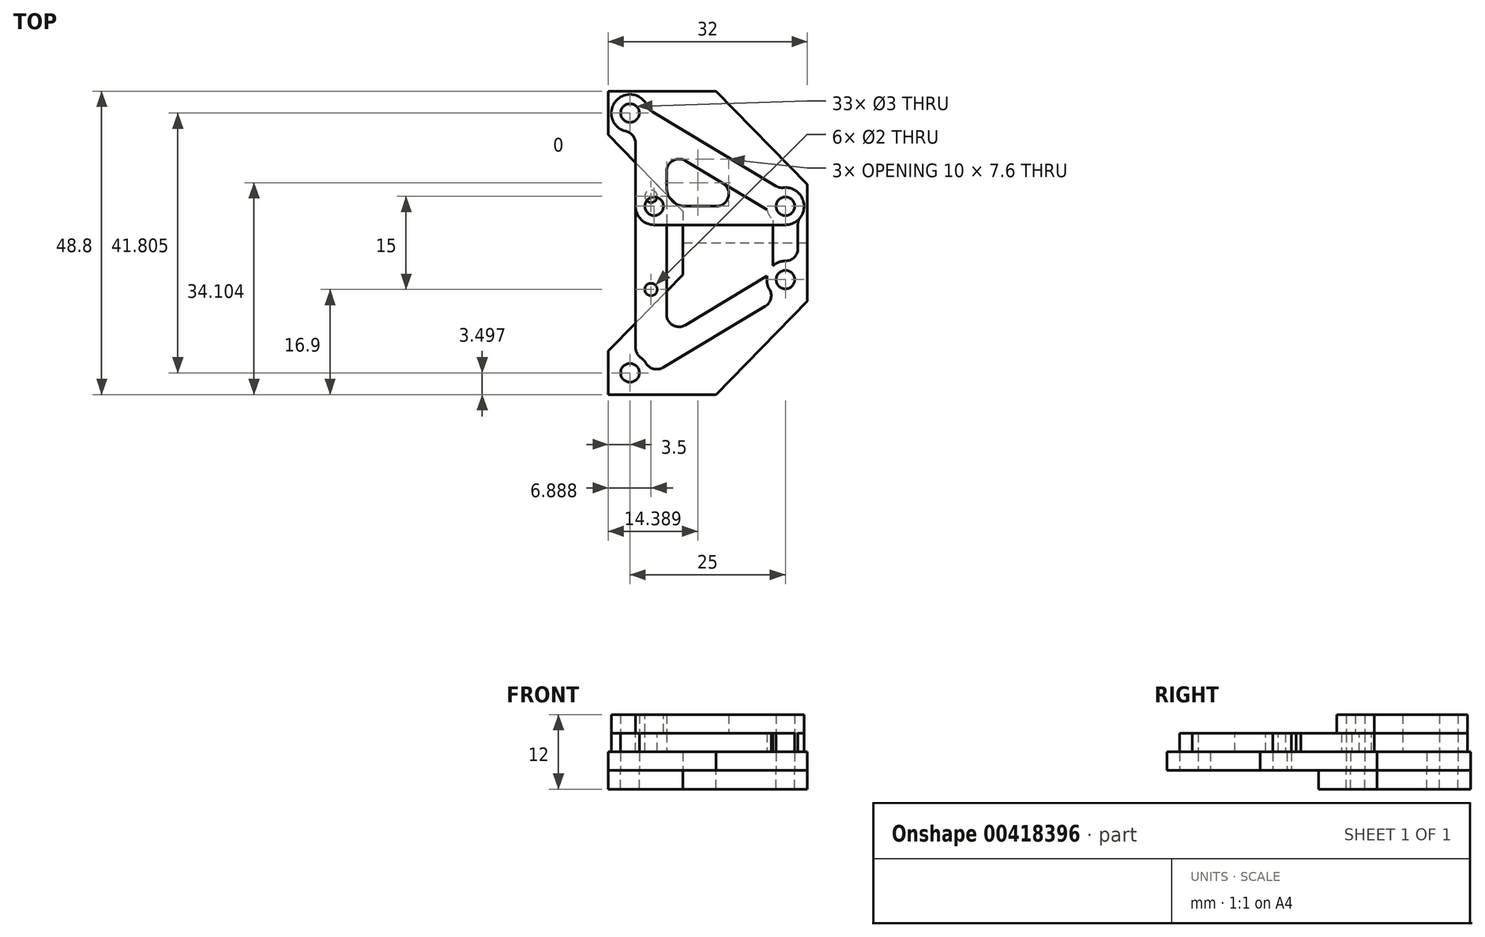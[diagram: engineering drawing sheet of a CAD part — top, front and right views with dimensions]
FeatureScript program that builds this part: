
annotation { "Feature Type Name" : "Feature", "Feature Type Description" : "" }
export const myFeature = defineFeature(function(context is Context, id is Id, definition is map)
    precondition{}
    {
        {
            var Q0;
            Q0=qCreatedBy(makeId("Top.planeOp"),FACE);
            var sketch = newSketch(context, id + "F0", { "sketchPlane" : qUnion([Q0])});
            skCircle(sketch, "E0", {"center": v(0, 20.9) * mm, "radius": 1.5 * mm});
            skCircle(sketch, "E1", {"center": v(25, 5.9) * mm, "radius": 1.5 * mm});
            skCircle(sketch, "E2.MirrorC", {"center": v(0, -20.9) * mm, "radius": 1.5 * mm});
            skCircle(sketch, "E3.MirrorC", {"center": v(25, -5.9) * mm, "radius": 1.5 * mm});
            skLineSegment(sketch, "E4", {"start": v(8.5, 5.12) * mm, "end": v(-3.5, 17.4) * mm});
            skLineSegment(sketch, "E5", {"start": v(-3.5, 17.4) * mm, "end": v(-3.5, 24.4) * mm});
            skLineSegment(sketch, "E6", {"start": v(-3.5, 24.4) * mm, "end": v(13.85, 24.4) * mm});
            skLineSegment(sketch, "E7", {"start": v(13.85, 24.4) * mm, "end": v(28.5, 9.4) * mm});
            skLineSegment(sketch, "E8", {"start": v(28.5, 9.4) * mm, "end": v(28.5, 0) * mm});
            skLineSegment(sketch, "E9.MirrorCS", {"start": v(8.5, -5.12) * mm, "end": v(-3.5, -17.4) * mm});
            skLineSegment(sketch, "E10.MirrorCS", {"start": v(-3.5, -17.4) * mm, "end": v(-3.5, -24.4) * mm});
            skLineSegment(sketch, "E11.MirrorCS", {"start": v(-3.5, -24.4) * mm, "end": v(13.85, -24.4) * mm});
            skLineSegment(sketch, "E12.MirrorCS", {"start": v(13.85, -24.4) * mm, "end": v(28.5, -9.4) * mm});
            skLineSegment(sketch, "E13.MirrorCS", {"start": v(28.5, -9.4) * mm, "end": v(28.5, 0) * mm});
            skLineSegment(sketch, "E14", {"start": v(8.5, 5.12) * mm, "end": v(8.5, -5.12) * mm});
            skPoint(sketch, "E15.orphan", {"position": v(13.5, 0) * mm});
            skLineSegment(sketch, "E16", {"start": v(8.5, 0) * mm, "end": v(28.5, 0) * mm});
            skSolve(sketch);
        }
        {
            var Q0;
            Q0=qSketchRegion(id+"F0",true);
            extrude(context, id + "F1", {"entities" : qUnion([Q0]), "depth" : 3 * mm, "offsetDistance" : 25 * mm});
        }
        {
            var Q0;
            Q0=makeQuery(id+"F0.imprint","IMPRINT",FACE,{"disambiguationData":[TD([[makeQuery(id+"F0.imprint","IMPRINT",EDGE,{"derivedFrom":sQuery(id+"F0.wireOp",EDGE,"E0")}),-1.0]])]});
            extrude(context, id + "F2", {"entities" : qUnion([Q0]), "oppositeDirection" : true, "depth" : 3 * mm, "offsetDistance" : 25 * mm});
        }
        {
            var Q0;
            Q0=makeQuery(id+"F1.opExtrude","CAP_FACE",FACE,{"disambiguationData":[OSD([sQuery(id+"F0.wireOp",EDGE,"E0"),sQuery(id+"F0.wireOp",EDGE,"E1"),sQuery(id+"F0.wireOp",EDGE,"E2.MirrorC"),sQuery(id+"F0.wireOp",EDGE,"E3.MirrorC"),sQuery(id+"F0.wireOp",EDGE,"E4"),sQuery(id+"F0.wireOp",EDGE,"E5"),sQuery(id+"F0.wireOp",EDGE,"E6"),sQuery(id+"F0.wireOp",EDGE,"E7"),sQuery(id+"F0.wireOp",EDGE,"E8"),sQuery(id+"F0.wireOp",EDGE,"E9.MirrorCS"),sQuery(id+"F0.wireOp",EDGE,"E10.MirrorCS"),sQuery(id+"F0.wireOp",EDGE,"E11.MirrorCS"),sQuery(id+"F0.wireOp",EDGE,"E12.MirrorCS"),sQuery(id+"F0.wireOp",EDGE,"E13.MirrorCS"),sQuery(id+"F0.wireOp",EDGE,"E14")])],"isStart":false});
            var sketch = newSketch(context, id + "F3", { "sketchPlane" : qUnion([Q0])});
            skCircle(sketch, "E17.0", {"center": v(0, 20.9) * mm, "radius": 1.5 * mm});
            skCircle(sketch, "E18.0", {"center": v(25, 5.9) * mm, "radius": 1.5 * mm});
            skCircle(sketch, "E19", {"center": v(0, 20.9) * mm, "radius": 3 * mm});
            skCircle(sketch, "E20", {"center": v(25, 5.9) * mm, "radius": 3 * mm});
            skPoint(sketch, "E21", {"position": v(1.5, 20.9) * mm});
            skPoint(sketch, "E22", {"position": v(3, 20.9) * mm});
            skPoint(sketch, "E23", {"position": v(26.5, 5.9) * mm});
            skPoint(sketch, "E24", {"position": v(28, 5.9) * mm});
            skLineSegment(sketch, "E25", {"start": v(0, 20.9) * mm, "end": v(25, 5.9) * mm, "construction": true});
            skCircle(sketch, "E26.0", {"center": v(25, -5.9) * mm, "radius": 1.5 * mm});
            skLineSegment(sketch, "E27", {"start": v(25, 5.9) * mm, "end": v(25, -5.9) * mm, "construction": true});
            skCircle(sketch, "E28.MirrorC", {"center": v(25, -5.9) * mm, "radius": 3 * mm});
            skCircle(sketch, "E29.MirrorC", {"center": v(0, -20.9) * mm, "radius": 3 * mm});
            skLineSegment(sketch, "E30", {"start": v(23, 3.67) * mm, "end": v(23, -3.67) * mm});
            skLineSegment(sketch, "E31.MirrorCS", {"start": v(27, 3.67) * mm, "end": v(27, -3.67) * mm});
            skLineSegment(sketch, "E32", {"start": v(0.89, 18.04) * mm, "end": v(22.05, 5.34) * mm});
            skLineSegment(sketch, "E33.MirrorCS", {"start": v(2.95, 21.47) * mm, "end": v(24.11, 8.77) * mm});
            skLineSegment(sketch, "E34.MirrorCS", {"start": v(0.89, -18.04) * mm, "end": v(22.05, -5.34) * mm});
            skLineSegment(sketch, "E35.MirrorCS", {"start": v(2.95, -21.47) * mm, "end": v(24.11, -8.77) * mm});
            skLineSegment(sketch, "E36", {"start": v(0.89, 18.04) * mm, "end": v(0.89, -18.04) * mm});
            skLineSegment(sketch, "E37", {"start": v(5.89, 15.04) * mm, "end": v(5.89, -15.04) * mm});
            skSolve(sketch);
        }
        {
            var Q0;
            Q0=makeQuery(id+"F3.imprint","IMPRINT",FACE,{"disambiguationData":[TD([[makeQuery(id+"F3.imprint","IMPRINT",EDGE,{"derivedFrom":sQuery(id+"F3.wireOp",EDGE,"E17.0")}),-1.0]])]});
            var Q1;
            Q1=makeQuery(id+"F3.imprint","IMPRINT",FACE,{"disambiguationData":[TD([[makeQuery(id+"F3.imprint","IMPRINT",EDGE,{"derivedFrom":makeQuery(id+"F1.opExtrude","CAP_EDGE",EDGE,{"disambiguationData":[OSD([sQuery(id+"F0.wireOp",EDGE,"E2.MirrorC")])],"isStart":false})}),1.0]])]});
            var Q2;
            {var subQ0=sQuery(id+"F3.wireOp",EDGE,"E30");Q2=makeQuery(id+"F3.imprint","IMPRINT",FACE,{"disambiguationData":[TD([[makeQuery(id+"F3.imprint","IMPRINT",EDGE,{"derivedFrom":subQ0}),1.0]])]});}
            var Q3;
            Q3=makeQuery(id+"F3.imprint","IMPRINT",FACE,{"disambiguationData":[TD([[makeQuery(id+"F3.imprint","IMPRINT",EDGE,{"derivedFrom":sQuery(id+"F3.wireOp",EDGE,"E18.0")}),-1.0]])]});
            var Q4;
            {var subQ6=sQuery(id+"F3.wireOp",EDGE,"E33.MirrorCS");Q4=makeQuery(id+"F3.imprint","IMPRINT",FACE,{"disambiguationData":[TD([[makeQuery(id+"F3.imprint","IMPRINT",EDGE,{"derivedFrom":subQ6}),-1.0]])]});}
            var Q5;
            Q5=makeQuery(id+"F3.imprint","IMPRINT",FACE,{"disambiguationData":[TD([[makeQuery(id+"F3.imprint","IMPRINT",EDGE,{"derivedFrom":sQuery(id+"F3.wireOp",EDGE,"E26.0")}),1.0]])]});
            var Q6;
            {var subQ6=sQuery(id+"F3.wireOp",EDGE,"E35.MirrorCS");Q6=makeQuery(id+"F3.imprint","IMPRINT",FACE,{"disambiguationData":[TD([[makeQuery(id+"F3.imprint","IMPRINT",EDGE,{"derivedFrom":subQ6}),1.0]])]});}
            var Q7;
            {var subQ1=sQuery(id+"F3.wireOp",EDGE,"E32");var subQ3=sQuery(id+"F3.wireOp",EDGE,"E37");var subQ4=makeQuery(id+"F3.imprint","INTERSECT",VERTEX,{"derivedFrom":[subQ1,subQ3]});Q7=makeQuery(id+"F3.imprint","IMPRINT",FACE,{"disambiguationData":[TD([[makeQuery(id+"F3.imprint","IMPRINT",EDGE,{"disambiguationData":[TD([[subQ4,-1.0]])],"derivedFrom":subQ3}),-1.0]])]});}
            var Q8;
            {var subQ1=sQuery(id+"F3.wireOp",EDGE,"E34.MirrorCS");var subQ3=sQuery(id+"F3.wireOp",EDGE,"E37");var subQ4=makeQuery(id+"F3.imprint","INTERSECT",VERTEX,{"derivedFrom":[subQ1,subQ3]});Q8=makeQuery(id+"F3.imprint","IMPRINT",FACE,{"disambiguationData":[TD([[makeQuery(id+"F3.imprint","IMPRINT",EDGE,{"disambiguationData":[TD([[subQ4,1.0]])],"derivedFrom":subQ3}),-1.0]])]});}
            var Q9;
            {var subQ0=sQuery(id+"F3.wireOp",EDGE,"E36");var subQ1=makeQuery(id+"F1.opExtrude","CAP_EDGE",EDGE,{"disambiguationData":[OSD([sQuery(id+"F0.wireOp",EDGE,"E4")])],"isStart":false});var subQ2=makeQuery(id+"F3.imprint","INTERSECT",VERTEX,{"derivedFrom":[subQ1,subQ0]});Q9=makeQuery(id+"F3.imprint","IMPRINT",FACE,{"disambiguationData":[TD([[makeQuery(id+"F3.imprint","IMPRINT",EDGE,{"disambiguationData":[TD([[subQ2,-1.0]])],"derivedFrom":subQ0}),1.0]])]});}
            extrude(context, id + "F4", {"entities" : qUnion([Q0, Q1, Q2, Q3, Q4, Q5, Q6, Q7, Q8, Q9]), "depth" : 3 * mm, "offsetDistance" : 25 * mm});
        }
        {
            var Q0;
            Q0=makeQuery(id+"F4.opExtrude","SWEPT_EDGE",EDGE,{"disambiguationData":[OSD([sQuery(id+"F3.wireOp",EDGE,"E19"),sQuery(id+"F3.wireOp",EDGE,"E32"),sQuery(id+"F3.wireOp",EDGE,"E36")])]});
            var Q1;
            Q1=makeQuery(id+"F4.opExtrude","SWEPT_EDGE",EDGE,{"disambiguationData":[OSD([sQuery(id+"F3.wireOp",EDGE,"E29.MirrorC"),sQuery(id+"F3.wireOp",EDGE,"E34.MirrorCS"),sQuery(id+"F3.wireOp",EDGE,"E36")])]});
            var Q2;
            Q2=makeQuery(id+"F4.opExtrude","SWEPT_EDGE",EDGE,{"disambiguationData":[OSD([sQuery(id+"F3.wireOp",EDGE,"E29.MirrorC"),sQuery(id+"F3.wireOp",EDGE,"E35.MirrorCS")])]});
            var Q3;
            Q3=makeQuery(id+"F4.opExtrude","SWEPT_EDGE",EDGE,{"disambiguationData":[OSD([sQuery(id+"F3.wireOp",EDGE,"E28.MirrorC"),sQuery(id+"F3.wireOp",EDGE,"E35.MirrorCS")])]});
            var Q4;
            Q4=makeQuery(id+"F4.opExtrude","SWEPT_EDGE",EDGE,{"disambiguationData":[OSD([sQuery(id+"F3.wireOp",EDGE,"E20"),sQuery(id+"F3.wireOp",EDGE,"E31.MirrorCS")])]});
            var Q5;
            Q5=makeQuery(id+"F4.opExtrude","SWEPT_EDGE",EDGE,{"disambiguationData":[OSD([sQuery(id+"F3.wireOp",EDGE,"E28.MirrorC"),sQuery(id+"F3.wireOp",EDGE,"E31.MirrorCS")])]});
            var Q6;
            Q6=makeQuery(id+"F4.opExtrude","SWEPT_EDGE",EDGE,{"disambiguationData":[OSD([sQuery(id+"F3.wireOp",EDGE,"E20"),sQuery(id+"F3.wireOp",EDGE,"E33.MirrorCS")])]});
            var Q7;
            Q7=makeQuery(id+"F4.opExtrude","SWEPT_EDGE",EDGE,{"disambiguationData":[OSD([sQuery(id+"F3.wireOp",EDGE,"E34.MirrorCS"),sQuery(id+"F3.wireOp",EDGE,"E37")])]});
            var Q8;
            Q8=makeQuery(id+"F4.opExtrude","SWEPT_EDGE",EDGE,{"disambiguationData":[OSD([sQuery(id+"F3.wireOp",EDGE,"E32"),sQuery(id+"F3.wireOp",EDGE,"E37")])]});
            var Q9;
            Q9=makeQuery(id+"F4.opExtrude","SWEPT_EDGE",EDGE,{"disambiguationData":[OSD([sQuery(id+"F3.wireOp",EDGE,"E19"),sQuery(id+"F3.wireOp",EDGE,"E33.MirrorCS")])]});
            fillet(context, id + "F5", {"entities" : qUnion([Q0, Q1, Q2, Q3, Q4, Q5, Q6, Q7, Q8, Q9]), "radius" : 2 * mm, "tangentPropagation" : true, "allowEdgeOverflow" : false});
        }
        {
            var Q0;
            Q0=makeQuery(id+"F4.opExtrude","CAP_FACE",FACE,{"disambiguationData":[OSD([sQuery(id+"F0.wireOp",EDGE,"E2.MirrorC"),sQuery(id+"F3.wireOp",EDGE,"E17.0"),sQuery(id+"F3.wireOp",EDGE,"E18.0"),sQuery(id+"F3.wireOp",EDGE,"E19"),sQuery(id+"F3.wireOp",EDGE,"E20"),sQuery(id+"F3.wireOp",EDGE,"E26.0"),sQuery(id+"F3.wireOp",EDGE,"E28.MirrorC"),sQuery(id+"F3.wireOp",EDGE,"E29.MirrorC"),sQuery(id+"F3.wireOp",EDGE,"E30"),sQuery(id+"F3.wireOp",EDGE,"E31.MirrorCS"),sQuery(id+"F3.wireOp",EDGE,"E32"),sQuery(id+"F3.wireOp",EDGE,"E33.MirrorCS"),sQuery(id+"F3.wireOp",EDGE,"E34.MirrorCS"),sQuery(id+"F3.wireOp",EDGE,"E35.MirrorCS"),sQuery(id+"F3.wireOp",EDGE,"E36"),sQuery(id+"F3.wireOp",EDGE,"E37")])],"isStart":false});
            var sketch = newSketch(context, id + "F6", { "sketchPlane" : qUnion([Q0])});
            skCircle(sketch, "E38.0", {"center": v(0, 20.9) * mm, "radius": 3 * mm});
            skCircle(sketch, "E39.0", {"center": v(0, 20.9) * mm, "radius": 1.5 * mm});
            skCircle(sketch, "E40.0", {"center": v(25, 5.9) * mm, "radius": 1.5 * mm});
            skCircle(sketch, "E41.0", {"center": v(25, 5.9) * mm, "radius": 3 * mm});
            skArc(sketch, "E42.0", {"start": v(3.6, 21.07) * mm, "mid": v(3.11, 21.49) * mm, "end": v(2.78, 22.03) * mm});
            skLineSegment(sketch, "E43.0", {"start": v(2.95, 21.47) * mm, "end": v(24.11, 8.77) * mm});
            skArc(sketch, "E44.0", {"start": v(24.7, 8.89) * mm, "mid": v(24.05, 8.92) * mm, "end": v(23.46, 9.16) * mm});
            skArc(sketch, "E45.0", {"start": v(-0.67, 17.98) * mm, "mid": v(0.45, 17.28) * mm, "end": v(0.89, 16.03) * mm});
            skLineSegment(sketch, "E46.0", {"start": v(0.89, 18.04) * mm, "end": v(0.89, 2.9) * mm});
            skArc(sketch, "E47.0", {"start": v(5.89, 11.5) * mm, "mid": v(6.9, 13.25) * mm, "end": v(8.92, 13.22) * mm});
            skLineSegment(sketch, "E48.0", {"start": v(5.89, 15.04) * mm, "end": v(5.89, 2.9) * mm});
            skLineSegment(sketch, "E49.0", {"start": v(0.89, 18.04) * mm, "end": v(14.92, 9.62) * mm});
            skLineSegment(sketch, "E50", {"start": v(25, 2.9) * mm, "end": v(5.89, 2.9) * mm});
            skLineSegment(sketch, "E51", {"start": v(5.89, 5.9) * mm, "end": v(13.9, 5.9) * mm});
            skLineSegment(sketch, "E52", {"start": v(5.89, 2.9) * mm, "end": v(0.89, 2.9) * mm});
            skPoint(sketch, "E53.orphan", {"position": v(0.89, -18.04) * mm});
            skPoint(sketch, "E54.orphan", {"position": v(5.89, -15.04) * mm});
            skPoint(sketch, "E55.newPointA", {"position": v(22.05, 5.34) * mm});
            skArc(sketch, "E55.filletArc", {"start": v(13.9, 5.9) * mm, "mid": v(15.82, 7.37) * mm, "end": v(14.92, 9.62) * mm});
            skSolve(sketch);
        }
        {
            var Q0;
            Q0=qSketchRegion(id+"F6",true);
            var Q1;
            {var subQ0=sQuery(id+"F6.wireOp",EDGE,"E47.0");Q1=makeQuery(id+"F6.imprint","IMPRINT",FACE,{"disambiguationData":[TD([[makeQuery(id+"F6.imprint","IMPRINT",EDGE,{"derivedFrom":subQ0}),1.0]])]});}
            extrude(context, id + "F7", {"entities" : qUnion([Q0, Q1]), "depth" : 3 * mm, "offsetDistance" : 25 * mm});
        }
        {
            var Q0;
            Q0=makeQuery(id+"F7.opExtrude","SWEPT_EDGE",EDGE,{"disambiguationData":[OSD([sQuery(id+"F6.wireOp",EDGE,"E48.0"),sQuery(id+"F6.wireOp",EDGE,"E51")])]});
            var Q1;
            Q1=makeQuery(id+"F7.opExtrude","SWEPT_EDGE",EDGE,{"disambiguationData":[OSD([sQuery(id+"F3.wireOp",EDGE,"E36"),sQuery(id+"F6.wireOp",EDGE,"E46.0"),sQuery(id+"F6.wireOp",EDGE,"E52")])]});
            fillet(context, id + "F8", {"entities" : qUnion([Q0, Q1]), "radius" : 3 * mm, "tangentPropagation" : true, "allowEdgeOverflow" : false});
        }
        {
            var Q0;
            Q0=makeQuery(id+"F4.opExtrude","CAP_FACE",FACE,{"disambiguationData":[OSD([sQuery(id+"F0.wireOp",EDGE,"E2.MirrorC"),sQuery(id+"F3.wireOp",EDGE,"E17.0"),sQuery(id+"F3.wireOp",EDGE,"E18.0"),sQuery(id+"F3.wireOp",EDGE,"E19"),sQuery(id+"F3.wireOp",EDGE,"E20"),sQuery(id+"F3.wireOp",EDGE,"E26.0"),sQuery(id+"F3.wireOp",EDGE,"E28.MirrorC"),sQuery(id+"F3.wireOp",EDGE,"E29.MirrorC"),sQuery(id+"F3.wireOp",EDGE,"E30"),sQuery(id+"F3.wireOp",EDGE,"E31.MirrorCS"),sQuery(id+"F3.wireOp",EDGE,"E32"),sQuery(id+"F3.wireOp",EDGE,"E33.MirrorCS"),sQuery(id+"F3.wireOp",EDGE,"E34.MirrorCS"),sQuery(id+"F3.wireOp",EDGE,"E35.MirrorCS"),sQuery(id+"F3.wireOp",EDGE,"E36"),sQuery(id+"F3.wireOp",EDGE,"E37")])],"isStart":false});
            var sketch = newSketch(context, id + "F9", { "sketchPlane" : qUnion([Q0])});
            skLineSegment(sketch, "E56", {"start": v(5.89, 0) * mm, "end": v(0.89, 0) * mm, "construction": true});
            skLineSegment(sketch, "E57", {"start": v(3.39, 0) * mm, "end": v(3.39, 16.03) * mm, "construction": true});
            skCircle(sketch, "E58", {"center": v(3.39, 7.5) * mm, "radius": 1 * mm});
            skCircle(sketch, "E59.MirrorC", {"center": v(3.39, -7.5) * mm, "radius": 1 * mm});
            skSolve(sketch);
        }
        {
            var Q0;
            Q0=qSketchRegion(id+"F9",true);
            extrude(context, id + "F10", {"entities" : qUnion([Q0]), "operationType" : NewBodyOperationType.REMOVE, "endBound" : BoundingType.UP_TO_NEXT, "oppositeDirection" : true, "depth" : 25 * mm, "offsetDistance" : 25 * mm});
        }
        {
            var Q0;
            Q0=makeQuery(id+"F7.opExtrude","CAP_FACE",FACE,{"disambiguationData":[OSD([sQuery(id+"F6.wireOp",EDGE,"E38.0"),sQuery(id+"F6.wireOp",EDGE,"E39.0"),sQuery(id+"F6.wireOp",EDGE,"E40.0"),sQuery(id+"F6.wireOp",EDGE,"E41.0"),sQuery(id+"F6.wireOp",EDGE,"E42.0"),sQuery(id+"F6.wireOp",EDGE,"E43.0"),sQuery(id+"F6.wireOp",EDGE,"E44.0"),sQuery(id+"F6.wireOp",EDGE,"E45.0"),sQuery(id+"F6.wireOp",EDGE,"E46.0"),sQuery(id+"F6.wireOp",EDGE,"E47.0"),sQuery(id+"F6.wireOp",EDGE,"E48.0"),sQuery(id+"F6.wireOp",EDGE,"E49.0"),sQuery(id+"F6.wireOp",EDGE,"E50"),sQuery(id+"F6.wireOp",EDGE,"E51"),sQuery(id+"F6.wireOp",EDGE,"E52"),sQuery(id+"F6.wireOp",EDGE,"E55.filletArc")])],"isStart":false});
            var sketch = newSketch(context, id + "F11", { "sketchPlane" : qUnion([Q0])});
            skArc(sketch, "E60.0", {"start": v(0.89, 5.9) * mm, "mid": v(1.77, 3.78) * mm, "end": v(3.89, 2.9) * mm, "construction": true});
            skCircle(sketch, "E61", {"center": v(3.89, 5.9) * mm, "radius": 1.5 * mm});
            skSolve(sketch);
        }
        {
            var Q0;
            Q0=qSketchRegion(id+"F11",true);
            extrude(context, id + "F12", {"entities" : qUnion([Q0]), "operationType" : NewBodyOperationType.REMOVE, "endBound" : BoundingType.UP_TO_NEXT, "oppositeDirection" : true, "depth" : 25 * mm, "offsetDistance" : 25 * mm});
        }
    });
